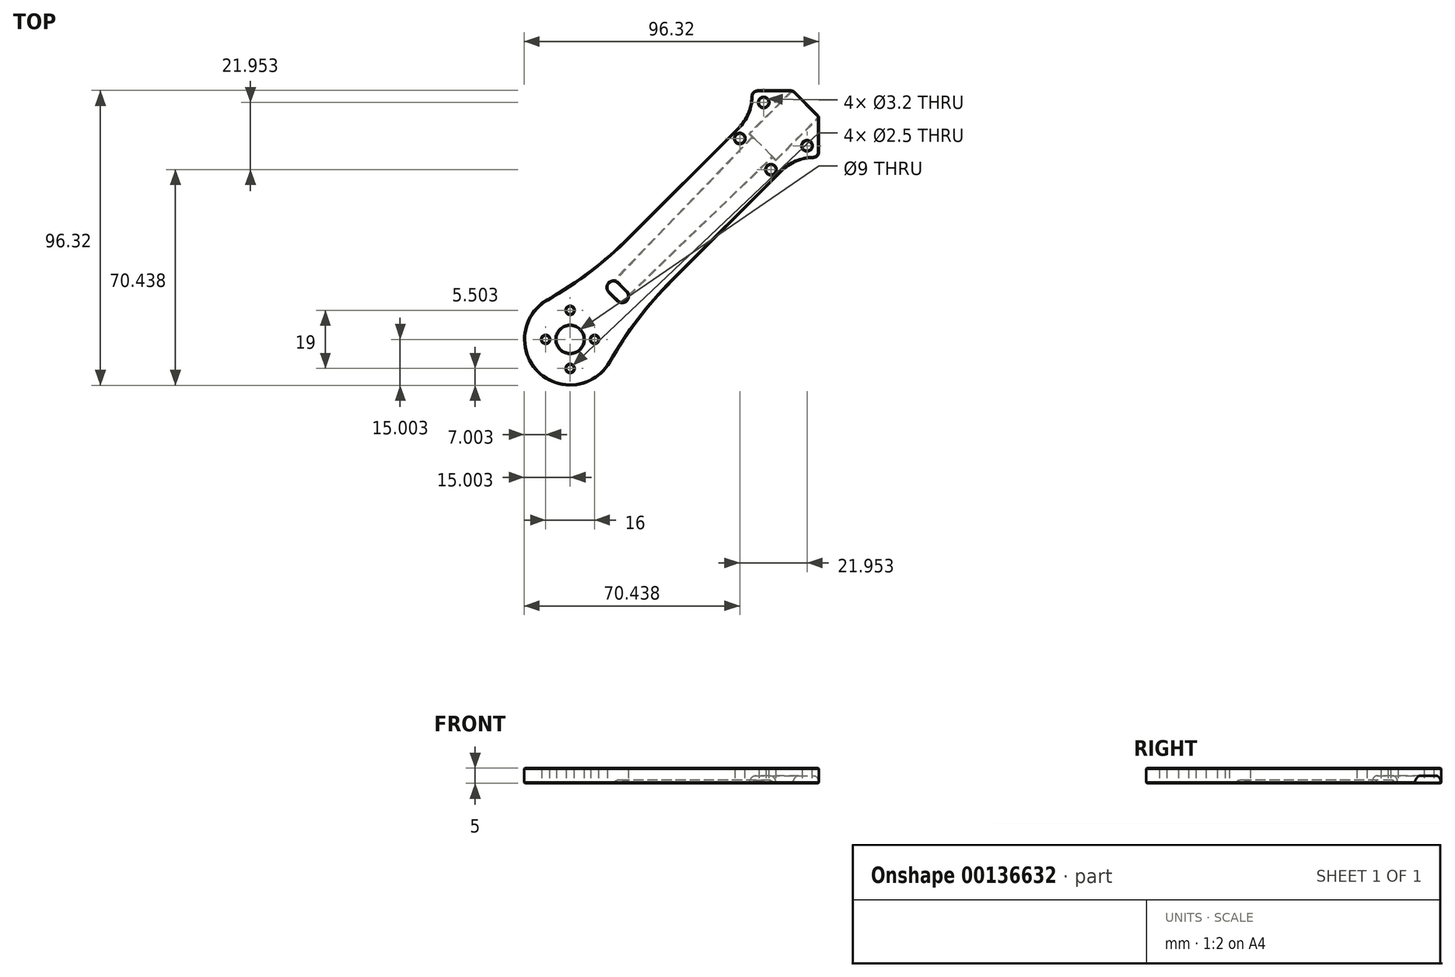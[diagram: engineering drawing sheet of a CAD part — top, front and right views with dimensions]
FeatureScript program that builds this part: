
annotation { "Feature Type Name" : "Feature", "Feature Type Description" : "" }
export const myFeature = defineFeature(function(context is Context, id is Id, definition is map)
    precondition{}
    {
        {
            var Q0;
            Q0=qCreatedBy(makeId("Top.planeOp"),FACE);
            var sketch = newSketch(context, id + "F0", { "sketchPlane" : qUnion([Q0])});
            skPoint(sketch, "E0.middle", {"position": v(0, 0) * mm});
            skCircle(sketch, "E1.MirrorC", {"center": v(-15, -15) * mm, "radius": 1.6 * mm, "construction": true});
            skCircle(sketch, "E2.MirrorC", {"center": v(-89.32, -81.32) * mm, "radius": 1.25 * mm});
            skCircle(sketch, "E3.MirrorC", {"center": v(-81.32, -71.82) * mm, "radius": 1.25 * mm});
            skCircle(sketch, "E4.MirrorC", {"center": v(-81.32, -90.82) * mm, "radius": 1.25 * mm});
            skCircle(sketch, "E5.MirrorC", {"center": v(-73.32, -81.32) * mm, "radius": 1.25 * mm});
            skCircle(sketch, "E6.MirrorC", {"center": v(-81.32, -81.32) * mm, "radius": 4.5 * mm});
            skCircle(sketch, "E7.MirrorC", {"center": v(-81.32, -81.32) * mm, "radius": 15 * mm});
            skLineSegment(sketch, "E8.MirrorCS", {"start": v(-22, -7.86) * mm, "end": v(-80.48, -66.34) * mm});
            skLineSegment(sketch, "E9.MirrorCS", {"start": v(-7.86, -22) * mm, "end": v(-66.34, -80.48) * mm});
            skLineSegment(sketch, "E10", {"start": v(0, -22) * mm, "end": v(-7.86, -22) * mm});
            skLineSegment(sketch, "E11", {"start": v(-22, 0) * mm, "end": v(-22, -7.86) * mm});
            skLineSegment(sketch, "E12", {"start": v(-22, -7.86) * mm, "end": v(-22, -22) * mm, "construction": true});
            skLineSegment(sketch, "E13", {"start": v(-7.86, -22) * mm, "end": v(-22, -22) * mm, "construction": true});
            skLineSegment(sketch, "E14", {"start": v(-8.49, 0) * mm, "end": v(-22.63, -14.14) * mm});
            skLineSegment(sketch, "E15", {"start": v(-22.63, -14.14) * mm, "end": v(-14.14, -22.63) * mm});
            skLineSegment(sketch, "E16", {"start": v(-14.14, -22.63) * mm, "end": v(0, -8.49) * mm});
            skLineSegment(sketch, "E17", {"start": v(-22, 0) * mm, "end": v(-8.49, 0) * mm});
            skLineSegment(sketch, "E18", {"start": v(0, -22) * mm, "end": v(0, -8.49) * mm});
            skLineSegment(sketch, "E19", {"start": v(-8.49, 0) * mm, "end": v(0, -8.49) * mm});
            skPoint(sketch, "E20", {"position": v(-18.38, -18.38) * mm});
            skPoint(sketch, "E21", {"position": v(-15.9, -20.86) * mm});
            skPoint(sketch, "E22", {"position": v(-20.86, -15.9) * mm});
            skLineSegment(sketch, "E23", {"start": v(-15, -15) * mm, "end": v(-81.32, -81.32) * mm, "construction": true});
            skPoint(sketch, "E24", {"position": v(-19.1, -17.68) * mm});
            skPoint(sketch, "E25", {"position": v(-17.68, -19.1) * mm});
            skPoint(sketch, "E26", {"position": v(-20.15, -16.62) * mm});
            skPoint(sketch, "E27", {"position": v(-21.57, -15.2) * mm});
            skPoint(sketch, "E28", {"position": v(-16.62, -20.15) * mm});
            skPoint(sketch, "E29", {"position": v(-15.2, -21.57) * mm});
            skLineSegment(sketch, "E30", {"start": v(-64.35, -64.35) * mm, "end": v(-65.76, -62.93) * mm});
            skLineSegment(sketch, "E31", {"start": v(-68.6, -62.93) * mm, "end": v(-68.6, -62.93) * mm});
            skLineSegment(sketch, "E32", {"start": v(-68.59, -65.76) * mm, "end": v(-67.18, -67.18) * mm});
            skLineSegment(sketch, "E33.MirrorCS", {"start": v(-64.35, -64.35) * mm, "end": v(-62.93, -65.76) * mm});
            skLineSegment(sketch, "E34.MirrorCS", {"start": v(-62.93, -68.6) * mm, "end": v(-62.93, -68.6) * mm});
            skLineSegment(sketch, "E35.MirrorCS", {"start": v(-65.76, -68.59) * mm, "end": v(-67.18, -67.18) * mm});
            skArc(sketch, "E36.filletArc", {"start": v(-65.76, -68.59) * mm, "mid": v(-64.35, -69.18) * mm, "end": v(-62.93, -68.6) * mm});
            skArc(sketch, "E37.filletArc", {"start": v(-68.6, -62.93) * mm, "mid": v(-69.18, -64.35) * mm, "end": v(-68.59, -65.76) * mm});
            skArc(sketch, "E38.filletArc", {"start": v(-65.76, -62.93) * mm, "mid": v(-67.18, -62.35) * mm, "end": v(-68.6, -62.93) * mm});
            skArc(sketch, "E39.filletArc", {"start": v(-62.93, -68.6) * mm, "mid": v(-62.35, -67.18) * mm, "end": v(-62.93, -65.76) * mm});
            skPoint(sketch, "E40", {"position": v(-67.04, -62.44) * mm});
            skLineSegment(sketch, "E41", {"start": v(-21.57, -15.2) * mm, "end": v(-67.04, -62.44) * mm});
            skPoint(sketch, "E42.MirrorP", {"position": v(-62.44, -67.04) * mm});
            skLineSegment(sketch, "E43.MirrorCS", {"start": v(-15.2, -21.57) * mm, "end": v(-62.44, -67.04) * mm});
            skLineSegment(sketch, "E44", {"start": v(-22, 0) * mm, "end": v(0, -22) * mm, "construction": true});
            skCircle(sketch, "E45", {"center": v(-18.07, -3.93) * mm, "radius": 1.6 * mm});
            skCircle(sketch, "E46.MirrorC", {"center": v(-3.93, -18.07) * mm, "radius": 1.6 * mm});
            skCircle(sketch, "E47", {"center": v(-15.7, -25.88) * mm, "radius": 1.6 * mm});
            skCircle(sketch, "E48.MirrorC", {"center": v(-25.88, -15.7) * mm, "radius": 1.6 * mm});
            skSolve(sketch);
        }
        {
            var Q0;
            Q0=makeQuery(id+"F0.imprint","IMPRINT",FACE,{"disambiguationData":[TD([[makeQuery(id+"F0.imprint","IMPRINT",EDGE,{"derivedFrom":sQuery(id+"F0.wireOp",EDGE,"E2.MirrorC")}),-1.0]])]});
            var Q1;
            {var subQ1=sQuery(id+"F0.wireOp",EDGE,"E8.MirrorCS");Q1=makeQuery(id+"F0.imprint","IMPRINT",FACE,{"disambiguationData":[TD([[makeQuery(id+"F0.imprint","IMPRINT",EDGE,{"derivedFrom":subQ1}),1.0]])]});}
            var Q2;
            Q2=makeQuery(id+"F0.imprint","IMPRINT",FACE,{"disambiguationData":[TD([[makeQuery(id+"F0.imprint","IMPRINT",EDGE,{"derivedFrom":sQuery(id+"F0.wireOp",EDGE,"E14")}),1.0]])]});
            var Q3;
            {var subQ0=sQuery(id+"F0.wireOp",EDGE,"spuSlL6A-g52Q-3iRA-Q68x-jWGHjwYxb2Ro");Q3=makeQuery(id+"F0.imprint","IMPRINT",FACE,{"disambiguationData":[TD([[makeQuery(id+"F0.imprint","IMPRINT",EDGE,{"derivedFrom":subQ0}),-1.0]])]});}
            var Q4;
            {var subQ0=sQuery(id+"F0.wireOp",EDGE,"nSd8rCcq-srJo-ZdqI-Aq73-i9T395iyRaMl");Q4=makeQuery(id+"F0.imprint","IMPRINT",FACE,{"disambiguationData":[TD([[makeQuery(id+"F0.imprint","IMPRINT",EDGE,{"derivedFrom":subQ0}),-1.0]])]});}
            var Q5;
            {var subQ0=sQuery(id+"F0.wireOp",EDGE,"IwZrl0sJ-2Pa8-YOrr-p6ua-zM0OcOKuCjxR");Q5=makeQuery(id+"F0.imprint","IMPRINT",FACE,{"disambiguationData":[TD([[makeQuery(id+"F0.imprint","IMPRINT",EDGE,{"derivedFrom":subQ0}),-1.0]])]});}
            var Q6;
            {var subQ0=sQuery(id+"F0.wireOp",EDGE,"iPaoqqKo-Xc6M-ub1s-4OOH-9ON20xjxPgdk");Q6=makeQuery(id+"F0.imprint","IMPRINT",FACE,{"disambiguationData":[TD([[makeQuery(id+"F0.imprint","IMPRINT",EDGE,{"derivedFrom":subQ0}),1.0]])]});}
            var Q7;
            {var subQ0=sQuery(id+"F0.wireOp",EDGE,"d5CYg6gf-SiJX-NEcw-N1Xb-WqFcHNI8gaRj");Q7=makeQuery(id+"F0.imprint","IMPRINT",FACE,{"disambiguationData":[TD([[makeQuery(id+"F0.imprint","IMPRINT",EDGE,{"derivedFrom":subQ0}),1.0]])]});}
            var Q8;
            {var subQ0=sQuery(id+"F0.wireOp",EDGE,"2Qdv7oXq-iKen-cdi0-Tvm3-qOwczSd402aX");Q8=makeQuery(id+"F0.imprint","IMPRINT",FACE,{"disambiguationData":[TD([[makeQuery(id+"F0.imprint","IMPRINT",EDGE,{"derivedFrom":subQ0}),1.0]])]});}
            var Q9;
            {var subQ0=sQuery(id+"F0.wireOp",EDGE,"N82YLeKA-DiP7-UTPM-TrJz-9M4YL49aT6VB");Q9=makeQuery(id+"F0.imprint","IMPRINT",FACE,{"disambiguationData":[TD([[makeQuery(id+"F0.imprint","IMPRINT",EDGE,{"derivedFrom":subQ0}),-1.0]])]});}
            var Q10;
            {var subQ0=sQuery(id+"F0.wireOp",EDGE,"N82YLeKA-DiP7-UTPM-TrJz-9M4YL49aT6VB");Q10=makeQuery(id+"F0.imprint","IMPRINT",FACE,{"disambiguationData":[TD([[makeQuery(id+"F0.imprint","IMPRINT",EDGE,{"derivedFrom":subQ0}),1.0]])]});}
            var Q11;
            {var subQ1=sQuery(id+"F0.wireOp",EDGE,"E30");Q11=makeQuery(id+"F0.imprint","IMPRINT",FACE,{"disambiguationData":[TD([[makeQuery(id+"F0.imprint","IMPRINT",EDGE,{"derivedFrom":subQ1}),-1.0]])]});}
            extrude(context, id + "F1", {"entities" : qUnion([Q0, Q1, Q2, Q3, Q4, Q5, Q6, Q7, Q8, Q9, Q10, Q11]), "depth" : 5 * mm});
        }
        {
            var Q0;
            Q0=makeQuery(id+"F1.opExtrude","SWEPT_EDGE",EDGE,{"disambiguationData":[OSD([sQuery(id+"F0.wireOp",EDGE,"E9.MirrorCS"),sQuery(id+"F0.wireOp",EDGE,"E10")])]});
            var Q1;
            Q1=makeQuery(id+"F1.opExtrude","SWEPT_EDGE",EDGE,{"disambiguationData":[OSD([sQuery(id+"F0.wireOp",EDGE,"E8.MirrorCS"),sQuery(id+"F0.wireOp",EDGE,"E11")])]});
            fillet(context, id + "F2", {"entities" : qUnion([Q0, Q1]), "radius" : 15 * mm, "tangentPropagation" : true, "allowEdgeOverflow" : false});
        }
        {
            var Q0;
            Q0=makeQuery(id+"F1.opExtrude","SWEPT_EDGE",EDGE,{"disambiguationData":[OSD([sQuery(id+"F0.wireOp",EDGE,"BRAAm4gB-HYyk-2Fgj-o60F-2sE3QVgur9YI"),sQuery(id+"F0.wireOp",EDGE,"E10")])]});
            var Q1;
            Q1=makeQuery(id+"F1.opExtrude","SWEPT_EDGE",EDGE,{"disambiguationData":[OSD([sQuery(id+"F0.wireOp",EDGE,"mTF9wQ4z-rhPj-fgc4-5pK7-IU84SbGBziMr"),sQuery(id+"F0.wireOp",EDGE,"E11")])]});
            var Q2;
            Q2=makeQuery(id+"F1.opExtrude","SWEPT_EDGE",EDGE,{"disambiguationData":[OSD([sQuery(id+"F0.wireOp",EDGE,"E16"),sQuery(id+"F0.wireOp",EDGE,"E18"),sQuery(id+"F0.wireOp",EDGE,"E19")])]});
            var Q3;
            Q3=makeQuery(id+"F1.opExtrude","SWEPT_EDGE",EDGE,{"disambiguationData":[OSD([sQuery(id+"F0.wireOp",EDGE,"E14"),sQuery(id+"F0.wireOp",EDGE,"E17"),sQuery(id+"F0.wireOp",EDGE,"E19")])]});
            fillet(context, id + "F3", {"entities" : qUnion([Q0, Q1, Q2, Q3]), "radius" : 2 * mm, "tangentPropagation" : true, "allowEdgeOverflow" : false});
        }
        {
            var Q0;
            Q0=makeQuery(id+"F1.opExtrude","SWEPT_EDGE",EDGE,{"disambiguationData":[OSD([sQuery(id+"F0.wireOp",EDGE,"E7.MirrorC"),sQuery(id+"F0.wireOp",EDGE,"E9.MirrorCS")])]});
            var Q1;
            Q1=makeQuery(id+"F1.opExtrude","SWEPT_EDGE",EDGE,{"disambiguationData":[OSD([sQuery(id+"F0.wireOp",EDGE,"E7.MirrorC"),sQuery(id+"F0.wireOp",EDGE,"E8.MirrorCS")])]});
            fillet(context, id + "F4", {"entities" : qUnion([Q0, Q1]), "radius" : 125 * mm, "tangentPropagation" : true, "allowEdgeOverflow" : false});
        }
        {
            var Q0;
            Q0=makeQuery(id+"F0.imprint","IMPRINT",FACE,{"disambiguationData":[TD([[makeQuery(id+"F0.imprint","IMPRINT",EDGE,{"derivedFrom":sQuery(id+"F0.wireOp",EDGE,"E14")}),1.0]])]});
            extrude(context, id + "F5", {"entities" : qUnion([Q0]), "operationType" : NewBodyOperationType.REMOVE, "depth" : 2.5 * mm});
        }
        {
            var Q0;
            Q0=makeQuery(id+"F5.boolean.opBoolean","COPY",EDGE,{"derivedFrom":makeQuery(id+"F5.opExtrude","CAP_EDGE",EDGE,{"disambiguationData":[OSD([sQuery(id+"F0.wireOp",EDGE,"E16")])],"isStart":false})});
            var Q1;
            Q1=makeQuery(id+"F5.boolean.opBoolean","COPY",EDGE,{"derivedFrom":makeQuery(id+"F5.opExtrude","CAP_EDGE",EDGE,{"disambiguationData":[OSD([sQuery(id+"F0.wireOp",EDGE,"E14")])],"isStart":false})});
            fillet(context, id + "F6", {"entities" : qUnion([Q0, Q1]), "radius" : 2.5 * mm, "tangentPropagation" : true, "allowEdgeOverflow" : false});
        }
        {
            var Q0;
            {var subQ1=sQuery(id+"F0.wireOp",EDGE,"E30");Q0=makeQuery(id+"F0.imprint","IMPRINT",FACE,{"disambiguationData":[TD([[makeQuery(id+"F0.imprint","IMPRINT",EDGE,{"derivedFrom":subQ1}),-1.0]])]});}
            extrude(context, id + "F7", {"entities" : qUnion([Q0]), "operationType" : NewBodyOperationType.REMOVE, "depth" : 1 * mm});
        }
        {
            var Q0;
            Q0=makeQuery(id+"F7.boolean.opBoolean","COPY",EDGE,{"derivedFrom":makeQuery(id+"F7.opExtrude","CAP_EDGE",EDGE,{"disambiguationData":[OSD([sQuery(id+"F0.wireOp",EDGE,"E43.MirrorCS")])],"isStart":false})});
            var Q1;
            Q1=makeQuery(id+"F7.boolean.opBoolean","COPY",EDGE,{"derivedFrom":makeQuery(id+"F7.opExtrude","CAP_EDGE",EDGE,{"disambiguationData":[OSD([sQuery(id+"F0.wireOp",EDGE,"E41")])],"isStart":false})});
            fillet(context, id + "F8", {"entities" : qUnion([Q0, Q1]), "radius" : 1 * mm, "tangentPropagation" : true, "allowEdgeOverflow" : false});
        }
        {
            var Q0;
            Q0=makeQuery(id+"F1.opExtrude","CAP_EDGE",EDGE,{"disambiguationData":[OSD([sQuery(id+"F0.wireOp",EDGE,"E36.filletArc"),sQuery(id+"F0.wireOp",EDGE,"E39.filletArc")])],"isStart":true});
            var Q1;
            Q1=makeQuery(id+"F1.opExtrude","CAP_EDGE",EDGE,{"disambiguationData":[OSD([sQuery(id+"F0.wireOp",EDGE,"E35.MirrorCS")])],"isStart":true});
            var Q2;
            Q2=makeQuery(id+"F1.opExtrude","CAP_EDGE",EDGE,{"disambiguationData":[OSD([sQuery(id+"F0.wireOp",EDGE,"E32")])],"isStart":true});
            var Q3;
            Q3=makeQuery(id+"F1.opExtrude","CAP_EDGE",EDGE,{"disambiguationData":[OSD([sQuery(id+"F0.wireOp",EDGE,"E37.filletArc"),sQuery(id+"F0.wireOp",EDGE,"E38.filletArc")])],"isStart":true});
            var Q4;
            Q4=makeQuery(id+"F7.boolean.opBoolean","COPY",EDGE,{"derivedFrom":makeQuery(id+"F7.opExtrude","CAP_EDGE",EDGE,{"disambiguationData":[OSD([sQuery(id+"F0.wireOp",EDGE,"E33.MirrorCS")])],"isStart":false})});
            var Q5;
            Q5=makeQuery(id+"F7.boolean.opBoolean","COPY",EDGE,{"derivedFrom":makeQuery(id+"F7.opExtrude","CAP_EDGE",EDGE,{"disambiguationData":[OSD([sQuery(id+"F0.wireOp",EDGE,"E30")])],"isStart":false})});
            var Q6;
            Q6=makeQuery(id+"F8.opFillet","BLEND_EDGE",EDGE,{"blendedFrom":[makeQuery(id+"F7.boolean.opBoolean","COPY",EDGE,{"derivedFrom":makeQuery(id+"F7.opExtrude","CAP_EDGE",EDGE,{"disambiguationData":[OSD([sQuery(id+"F0.wireOp",EDGE,"E43.MirrorCS")])],"isStart":false})}),makeQuery(id+"F1.opExtrude","CAP_FACE",FACE,{"disambiguationData":[OSD([sQuery(id+"F0.wireOp",EDGE,"E2.MirrorC"),sQuery(id+"F0.wireOp",EDGE,"E3.MirrorC"),sQuery(id+"F0.wireOp",EDGE,"E4.MirrorC"),sQuery(id+"F0.wireOp",EDGE,"E5.MirrorC"),sQuery(id+"F0.wireOp",EDGE,"E6.MirrorC"),sQuery(id+"F0.wireOp",EDGE,"E7.MirrorC"),sQuery(id+"F0.wireOp",EDGE,"E8.MirrorCS"),sQuery(id+"F0.wireOp",EDGE,"E9.MirrorCS"),sQuery(id+"F0.wireOp",EDGE,"E10"),sQuery(id+"F0.wireOp",EDGE,"E11"),sQuery(id+"F0.wireOp",EDGE,"E17"),sQuery(id+"F0.wireOp",EDGE,"E18"),sQuery(id+"F0.wireOp",EDGE,"E19"),sQuery(id+"F0.wireOp",EDGE,"E30"),sQuery(id+"F0.wireOp",EDGE,"E32"),sQuery(id+"F0.wireOp",EDGE,"E33.MirrorCS"),sQuery(id+"F0.wireOp",EDGE,"E35.MirrorCS"),sQuery(id+"F0.wireOp",EDGE,"E36.filletArc"),sQuery(id+"F0.wireOp",EDGE,"E37.filletArc"),sQuery(id+"F0.wireOp",EDGE,"E38.filletArc"),sQuery(id+"F0.wireOp",EDGE,"E39.filletArc")])],"isStart":true})],"blendedInto":[makeQuery(id+"F1.opExtrude","CAP_FACE",FACE,{"disambiguationData":[OSD([sQuery(id+"F0.wireOp",EDGE,"E2.MirrorC"),sQuery(id+"F0.wireOp",EDGE,"E3.MirrorC"),sQuery(id+"F0.wireOp",EDGE,"E4.MirrorC"),sQuery(id+"F0.wireOp",EDGE,"E5.MirrorC"),sQuery(id+"F0.wireOp",EDGE,"E6.MirrorC"),sQuery(id+"F0.wireOp",EDGE,"E7.MirrorC"),sQuery(id+"F0.wireOp",EDGE,"E8.MirrorCS"),sQuery(id+"F0.wireOp",EDGE,"E9.MirrorCS"),sQuery(id+"F0.wireOp",EDGE,"E10"),sQuery(id+"F0.wireOp",EDGE,"E11"),sQuery(id+"F0.wireOp",EDGE,"E17"),sQuery(id+"F0.wireOp",EDGE,"E18"),sQuery(id+"F0.wireOp",EDGE,"E19"),sQuery(id+"F0.wireOp",EDGE,"E30"),sQuery(id+"F0.wireOp",EDGE,"E32"),sQuery(id+"F0.wireOp",EDGE,"E33.MirrorCS"),sQuery(id+"F0.wireOp",EDGE,"E35.MirrorCS"),sQuery(id+"F0.wireOp",EDGE,"E36.filletArc"),sQuery(id+"F0.wireOp",EDGE,"E37.filletArc"),sQuery(id+"F0.wireOp",EDGE,"E38.filletArc"),sQuery(id+"F0.wireOp",EDGE,"E39.filletArc")])],"isStart":true})]});
            var Q7;
            Q7=makeQuery(id+"F8.opFillet","BLEND_EDGE",EDGE,{"blendedFrom":[makeQuery(id+"F7.boolean.opBoolean","COPY",EDGE,{"derivedFrom":makeQuery(id+"F7.opExtrude","CAP_EDGE",EDGE,{"disambiguationData":[OSD([sQuery(id+"F0.wireOp",EDGE,"E41")])],"isStart":false})}),makeQuery(id+"F1.opExtrude","CAP_FACE",FACE,{"disambiguationData":[OSD([sQuery(id+"F0.wireOp",EDGE,"E2.MirrorC"),sQuery(id+"F0.wireOp",EDGE,"E3.MirrorC"),sQuery(id+"F0.wireOp",EDGE,"E4.MirrorC"),sQuery(id+"F0.wireOp",EDGE,"E5.MirrorC"),sQuery(id+"F0.wireOp",EDGE,"E6.MirrorC"),sQuery(id+"F0.wireOp",EDGE,"E7.MirrorC"),sQuery(id+"F0.wireOp",EDGE,"E8.MirrorCS"),sQuery(id+"F0.wireOp",EDGE,"E9.MirrorCS"),sQuery(id+"F0.wireOp",EDGE,"E10"),sQuery(id+"F0.wireOp",EDGE,"E11"),sQuery(id+"F0.wireOp",EDGE,"E17"),sQuery(id+"F0.wireOp",EDGE,"E18"),sQuery(id+"F0.wireOp",EDGE,"E19"),sQuery(id+"F0.wireOp",EDGE,"E30"),sQuery(id+"F0.wireOp",EDGE,"E32"),sQuery(id+"F0.wireOp",EDGE,"E33.MirrorCS"),sQuery(id+"F0.wireOp",EDGE,"E35.MirrorCS"),sQuery(id+"F0.wireOp",EDGE,"E36.filletArc"),sQuery(id+"F0.wireOp",EDGE,"E37.filletArc"),sQuery(id+"F0.wireOp",EDGE,"E38.filletArc"),sQuery(id+"F0.wireOp",EDGE,"E39.filletArc")])],"isStart":true})],"blendedInto":[makeQuery(id+"F1.opExtrude","CAP_FACE",FACE,{"disambiguationData":[OSD([sQuery(id+"F0.wireOp",EDGE,"E2.MirrorC"),sQuery(id+"F0.wireOp",EDGE,"E3.MirrorC"),sQuery(id+"F0.wireOp",EDGE,"E4.MirrorC"),sQuery(id+"F0.wireOp",EDGE,"E5.MirrorC"),sQuery(id+"F0.wireOp",EDGE,"E6.MirrorC"),sQuery(id+"F0.wireOp",EDGE,"E7.MirrorC"),sQuery(id+"F0.wireOp",EDGE,"E8.MirrorCS"),sQuery(id+"F0.wireOp",EDGE,"E9.MirrorCS"),sQuery(id+"F0.wireOp",EDGE,"E10"),sQuery(id+"F0.wireOp",EDGE,"E11"),sQuery(id+"F0.wireOp",EDGE,"E17"),sQuery(id+"F0.wireOp",EDGE,"E18"),sQuery(id+"F0.wireOp",EDGE,"E19"),sQuery(id+"F0.wireOp",EDGE,"E30"),sQuery(id+"F0.wireOp",EDGE,"E32"),sQuery(id+"F0.wireOp",EDGE,"E33.MirrorCS"),sQuery(id+"F0.wireOp",EDGE,"E35.MirrorCS"),sQuery(id+"F0.wireOp",EDGE,"E36.filletArc"),sQuery(id+"F0.wireOp",EDGE,"E37.filletArc"),sQuery(id+"F0.wireOp",EDGE,"E38.filletArc"),sQuery(id+"F0.wireOp",EDGE,"E39.filletArc")])],"isStart":true})]});
            var Q8;
            Q8=makeQuery(id+"F6.opFillet","BLEND_EDGE",EDGE,{"blendedFrom":[makeQuery(id+"F5.boolean.opBoolean","COPY",EDGE,{"derivedFrom":makeQuery(id+"F5.opExtrude","CAP_EDGE",EDGE,{"disambiguationData":[OSD([sQuery(id+"F0.wireOp",EDGE,"E16")])],"isStart":false})}),makeQuery(id+"F1.opExtrude","CAP_FACE",FACE,{"disambiguationData":[OSD([sQuery(id+"F0.wireOp",EDGE,"E2.MirrorC"),sQuery(id+"F0.wireOp",EDGE,"E3.MirrorC"),sQuery(id+"F0.wireOp",EDGE,"E4.MirrorC"),sQuery(id+"F0.wireOp",EDGE,"E5.MirrorC"),sQuery(id+"F0.wireOp",EDGE,"E6.MirrorC"),sQuery(id+"F0.wireOp",EDGE,"E7.MirrorC"),sQuery(id+"F0.wireOp",EDGE,"E8.MirrorCS"),sQuery(id+"F0.wireOp",EDGE,"E9.MirrorCS"),sQuery(id+"F0.wireOp",EDGE,"E10"),sQuery(id+"F0.wireOp",EDGE,"E11"),sQuery(id+"F0.wireOp",EDGE,"E17"),sQuery(id+"F0.wireOp",EDGE,"E18"),sQuery(id+"F0.wireOp",EDGE,"E19"),sQuery(id+"F0.wireOp",EDGE,"E30"),sQuery(id+"F0.wireOp",EDGE,"E32"),sQuery(id+"F0.wireOp",EDGE,"E33.MirrorCS"),sQuery(id+"F0.wireOp",EDGE,"E35.MirrorCS"),sQuery(id+"F0.wireOp",EDGE,"E36.filletArc"),sQuery(id+"F0.wireOp",EDGE,"E37.filletArc"),sQuery(id+"F0.wireOp",EDGE,"E38.filletArc"),sQuery(id+"F0.wireOp",EDGE,"E39.filletArc")])],"isStart":true})],"blendedInto":[makeQuery(id+"F1.opExtrude","CAP_FACE",FACE,{"disambiguationData":[OSD([sQuery(id+"F0.wireOp",EDGE,"E2.MirrorC"),sQuery(id+"F0.wireOp",EDGE,"E3.MirrorC"),sQuery(id+"F0.wireOp",EDGE,"E4.MirrorC"),sQuery(id+"F0.wireOp",EDGE,"E5.MirrorC"),sQuery(id+"F0.wireOp",EDGE,"E6.MirrorC"),sQuery(id+"F0.wireOp",EDGE,"E7.MirrorC"),sQuery(id+"F0.wireOp",EDGE,"E8.MirrorCS"),sQuery(id+"F0.wireOp",EDGE,"E9.MirrorCS"),sQuery(id+"F0.wireOp",EDGE,"E10"),sQuery(id+"F0.wireOp",EDGE,"E11"),sQuery(id+"F0.wireOp",EDGE,"E17"),sQuery(id+"F0.wireOp",EDGE,"E18"),sQuery(id+"F0.wireOp",EDGE,"E19"),sQuery(id+"F0.wireOp",EDGE,"E30"),sQuery(id+"F0.wireOp",EDGE,"E32"),sQuery(id+"F0.wireOp",EDGE,"E33.MirrorCS"),sQuery(id+"F0.wireOp",EDGE,"E35.MirrorCS"),sQuery(id+"F0.wireOp",EDGE,"E36.filletArc"),sQuery(id+"F0.wireOp",EDGE,"E37.filletArc"),sQuery(id+"F0.wireOp",EDGE,"E38.filletArc"),sQuery(id+"F0.wireOp",EDGE,"E39.filletArc")])],"isStart":true})]});
            var Q9;
            Q9=makeQuery(id+"F6.opFillet","BLEND_EDGE",EDGE,{"blendedFrom":[makeQuery(id+"F5.boolean.opBoolean","COPY",EDGE,{"derivedFrom":makeQuery(id+"F5.opExtrude","CAP_EDGE",EDGE,{"disambiguationData":[OSD([sQuery(id+"F0.wireOp",EDGE,"E14")])],"isStart":false})}),makeQuery(id+"F1.opExtrude","CAP_FACE",FACE,{"disambiguationData":[OSD([sQuery(id+"F0.wireOp",EDGE,"E2.MirrorC"),sQuery(id+"F0.wireOp",EDGE,"E3.MirrorC"),sQuery(id+"F0.wireOp",EDGE,"E4.MirrorC"),sQuery(id+"F0.wireOp",EDGE,"E5.MirrorC"),sQuery(id+"F0.wireOp",EDGE,"E6.MirrorC"),sQuery(id+"F0.wireOp",EDGE,"E7.MirrorC"),sQuery(id+"F0.wireOp",EDGE,"E8.MirrorCS"),sQuery(id+"F0.wireOp",EDGE,"E9.MirrorCS"),sQuery(id+"F0.wireOp",EDGE,"E10"),sQuery(id+"F0.wireOp",EDGE,"E11"),sQuery(id+"F0.wireOp",EDGE,"E17"),sQuery(id+"F0.wireOp",EDGE,"E18"),sQuery(id+"F0.wireOp",EDGE,"E19"),sQuery(id+"F0.wireOp",EDGE,"E30"),sQuery(id+"F0.wireOp",EDGE,"E32"),sQuery(id+"F0.wireOp",EDGE,"E33.MirrorCS"),sQuery(id+"F0.wireOp",EDGE,"E35.MirrorCS"),sQuery(id+"F0.wireOp",EDGE,"E36.filletArc"),sQuery(id+"F0.wireOp",EDGE,"E37.filletArc"),sQuery(id+"F0.wireOp",EDGE,"E38.filletArc"),sQuery(id+"F0.wireOp",EDGE,"E39.filletArc")])],"isStart":true})],"blendedInto":[makeQuery(id+"F1.opExtrude","CAP_FACE",FACE,{"disambiguationData":[OSD([sQuery(id+"F0.wireOp",EDGE,"E2.MirrorC"),sQuery(id+"F0.wireOp",EDGE,"E3.MirrorC"),sQuery(id+"F0.wireOp",EDGE,"E4.MirrorC"),sQuery(id+"F0.wireOp",EDGE,"E5.MirrorC"),sQuery(id+"F0.wireOp",EDGE,"E6.MirrorC"),sQuery(id+"F0.wireOp",EDGE,"E7.MirrorC"),sQuery(id+"F0.wireOp",EDGE,"E8.MirrorCS"),sQuery(id+"F0.wireOp",EDGE,"E9.MirrorCS"),sQuery(id+"F0.wireOp",EDGE,"E10"),sQuery(id+"F0.wireOp",EDGE,"E11"),sQuery(id+"F0.wireOp",EDGE,"E17"),sQuery(id+"F0.wireOp",EDGE,"E18"),sQuery(id+"F0.wireOp",EDGE,"E19"),sQuery(id+"F0.wireOp",EDGE,"E30"),sQuery(id+"F0.wireOp",EDGE,"E32"),sQuery(id+"F0.wireOp",EDGE,"E33.MirrorCS"),sQuery(id+"F0.wireOp",EDGE,"E35.MirrorCS"),sQuery(id+"F0.wireOp",EDGE,"E36.filletArc"),sQuery(id+"F0.wireOp",EDGE,"E37.filletArc"),sQuery(id+"F0.wireOp",EDGE,"E38.filletArc"),sQuery(id+"F0.wireOp",EDGE,"E39.filletArc")])],"isStart":true})]});
            var Q10;
            Q10=makeQuery(id+"F7.boolean.opBoolean","COPY",EDGE,{"derivedFrom":makeQuery(id+"F7.opExtrude","CAP_EDGE",EDGE,{"disambiguationData":[OSD([sQuery(id+"F0.wireOp",EDGE,"E15")])],"isStart":false})});
            var Q11;
            {var subQ0=sQuery(id+"F0.wireOp",EDGE,"E15");Q11=makeQuery(id+"F7.boolean.opBoolean","SPLIT",EDGE,{"disambiguationData":[TD([makeQuery(id+"F6.opFillet","BLEND_FACE",FACE,{"disambiguationData":[OSD([sQuery(id+"F0.wireOp",EDGE,"E16")])]})])],"derivedFrom":makeQuery(id+"F5.boolean.opBoolean","COPY",EDGE,{"derivedFrom":makeQuery(id+"F5.opExtrude","CAP_EDGE",EDGE,{"disambiguationData":[OSD([subQ0])],"isStart":true})})});}
            var Q12;
            {var subQ0=sQuery(id+"F0.wireOp",EDGE,"E15");Q12=makeQuery(id+"F7.boolean.opBoolean","SPLIT",EDGE,{"disambiguationData":[TD([makeQuery(id+"F6.opFillet","BLEND_FACE",FACE,{"disambiguationData":[OSD([sQuery(id+"F0.wireOp",EDGE,"E14")])]})])],"derivedFrom":makeQuery(id+"F5.boolean.opBoolean","COPY",EDGE,{"derivedFrom":makeQuery(id+"F5.opExtrude","CAP_EDGE",EDGE,{"disambiguationData":[OSD([subQ0])],"isStart":true})})});}
            var Q13;
            Q13=makeQuery(id+"F5.boolean.opBoolean","COPY",EDGE,{"derivedFrom":makeQuery(id+"F5.opExtrude","CAP_EDGE",EDGE,{"disambiguationData":[OSD([sQuery(id+"F0.wireOp",EDGE,"E19")])],"isStart":false})});
            var Q14;
            Q14=makeQuery(id+"F1.opExtrude","CAP_FACE",FACE,{"disambiguationData":[OSD([sQuery(id+"F0.wireOp",EDGE,"E2.MirrorC"),sQuery(id+"F0.wireOp",EDGE,"E3.MirrorC"),sQuery(id+"F0.wireOp",EDGE,"E4.MirrorC"),sQuery(id+"F0.wireOp",EDGE,"E5.MirrorC"),sQuery(id+"F0.wireOp",EDGE,"E6.MirrorC"),sQuery(id+"F0.wireOp",EDGE,"E7.MirrorC"),sQuery(id+"F0.wireOp",EDGE,"E8.MirrorCS"),sQuery(id+"F0.wireOp",EDGE,"E9.MirrorCS"),sQuery(id+"F0.wireOp",EDGE,"E10"),sQuery(id+"F0.wireOp",EDGE,"E11"),sQuery(id+"F0.wireOp",EDGE,"E17"),sQuery(id+"F0.wireOp",EDGE,"E18"),sQuery(id+"F0.wireOp",EDGE,"E19"),sQuery(id+"F0.wireOp",EDGE,"E30"),sQuery(id+"F0.wireOp",EDGE,"E32"),sQuery(id+"F0.wireOp",EDGE,"E33.MirrorCS"),sQuery(id+"F0.wireOp",EDGE,"E35.MirrorCS"),sQuery(id+"F0.wireOp",EDGE,"E36.filletArc"),sQuery(id+"F0.wireOp",EDGE,"E37.filletArc"),sQuery(id+"F0.wireOp",EDGE,"E38.filletArc"),sQuery(id+"F0.wireOp",EDGE,"E39.filletArc")])],"isStart":false});
            var Q15;
            Q15=makeQuery(id+"F1.opExtrude","CAP_FACE",FACE,{"disambiguationData":[OSD([sQuery(id+"F0.wireOp",EDGE,"E2.MirrorC"),sQuery(id+"F0.wireOp",EDGE,"E3.MirrorC"),sQuery(id+"F0.wireOp",EDGE,"E4.MirrorC"),sQuery(id+"F0.wireOp",EDGE,"E5.MirrorC"),sQuery(id+"F0.wireOp",EDGE,"E6.MirrorC"),sQuery(id+"F0.wireOp",EDGE,"E7.MirrorC"),sQuery(id+"F0.wireOp",EDGE,"E8.MirrorCS"),sQuery(id+"F0.wireOp",EDGE,"E9.MirrorCS"),sQuery(id+"F0.wireOp",EDGE,"E10"),sQuery(id+"F0.wireOp",EDGE,"E11"),sQuery(id+"F0.wireOp",EDGE,"E17"),sQuery(id+"F0.wireOp",EDGE,"E18"),sQuery(id+"F0.wireOp",EDGE,"E19"),sQuery(id+"F0.wireOp",EDGE,"E30"),sQuery(id+"F0.wireOp",EDGE,"E32"),sQuery(id+"F0.wireOp",EDGE,"E33.MirrorCS"),sQuery(id+"F0.wireOp",EDGE,"E35.MirrorCS"),sQuery(id+"F0.wireOp",EDGE,"E36.filletArc"),sQuery(id+"F0.wireOp",EDGE,"E37.filletArc"),sQuery(id+"F0.wireOp",EDGE,"E38.filletArc"),sQuery(id+"F0.wireOp",EDGE,"E39.filletArc")])],"isStart":true});
            chamfer(context, id + "F9", {"entities" : qUnion([Q0, Q1, Q2, Q3, Q4, Q5, Q6, Q7, Q8, Q9, Q10, Q11, Q12, Q13, Q14, Q15]), "width" : .25 * mm, "tangentPropagation" : true});
        }
    });
